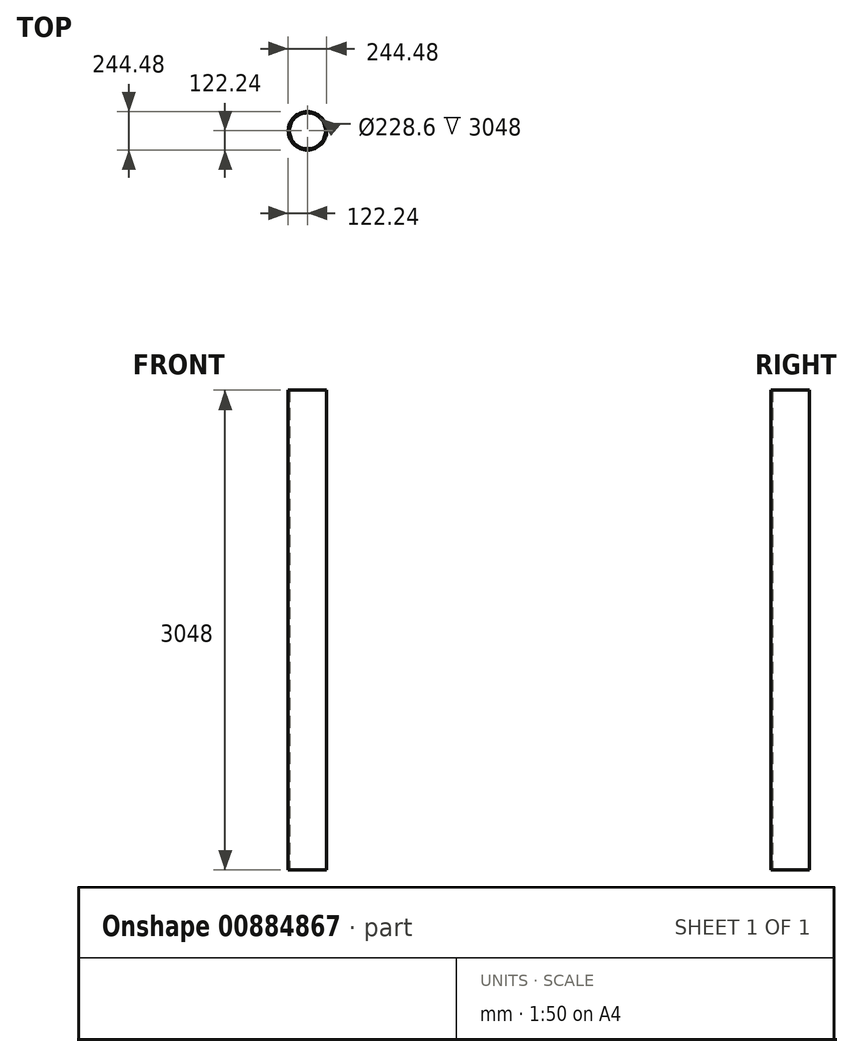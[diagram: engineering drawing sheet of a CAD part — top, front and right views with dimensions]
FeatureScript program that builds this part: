
annotation { "Feature Type Name" : "Feature", "Feature Type Description" : "" }
export const myFeature = defineFeature(function(context is Context, id is Id, definition is map)
    precondition{}
    {
        {
            var Q0;
            Q0=qCreatedBy(makeId("Top.planeOp"),FACE);
            var sketch = newSketch(context, id + "F0", { "sketchPlane" : qUnion([Q0])});
            skCircle(sketch, "E0", {"center": v(0, 0) * mm, "radius": 122.24 * mm});
            skCircle(sketch, "E1", {"center": v(0, 0) * mm, "radius": 114.3 * mm});
            skSolve(sketch);
        }
        {
            var Q0;
            Q0=makeQuery(id+"F0.imprint","IMPRINT",FACE,{"disambiguationData":[TD([[makeQuery(id+"F0.imprint","IMPRINT",EDGE,{"derivedFrom":sQuery(id+"F0.wireOp",EDGE,"E0")}),1.0]])]});
            extrude(context, id + "F1", {"entities" : qUnion([Q0]), "depth" : 3048 * mm, "offsetDistance" : 25.4 * mm});
        }
    });
